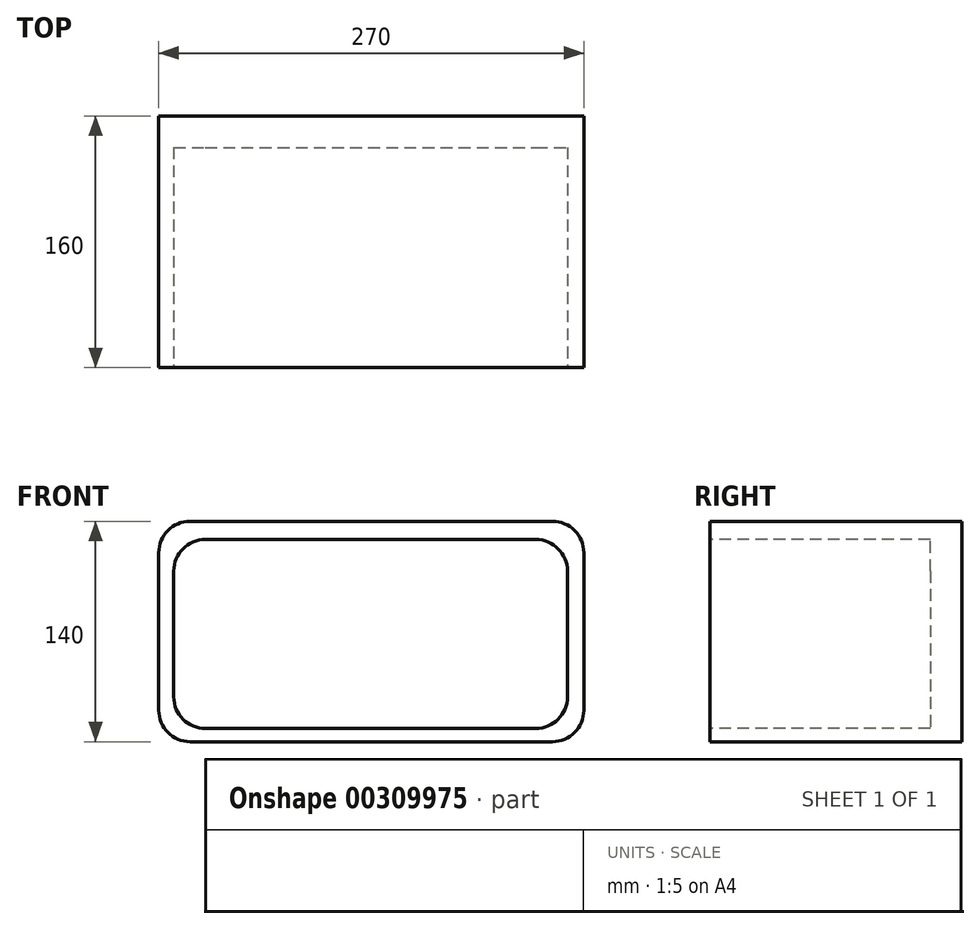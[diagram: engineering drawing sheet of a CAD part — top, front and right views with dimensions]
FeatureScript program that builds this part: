
annotation { "Feature Type Name" : "Feature", "Feature Type Description" : "" }
export const myFeature = defineFeature(function(context is Context, id is Id, definition is map)
    precondition{}
    {
        {
            var Q0;
            Q0=qCreatedBy(makeId("Front.planeOp"),FACE);
            var sketch = newSketch(context, id + "F0", { "sketchPlane" : qUnion([Q0])});
            skLineSegment(sketch, "E0.bottom", {"start": v(-135, 70) * mm, "end": v(135, 70) * mm});
            skLineSegment(sketch, "E0.top", {"start": v(-135, -70) * mm, "end": v(135, -70) * mm});
            skLineSegment(sketch, "E0.left", {"start": v(-135, 70) * mm, "end": v(-135, -70) * mm});
            skLineSegment(sketch, "E0.right", {"start": v(135, 70) * mm, "end": v(135, -70) * mm});
            skPoint(sketch, "E0.middle", {"position": v(0, 0) * mm});
            skSolve(sketch);
        }
        {
            var Q0;
            Q0=qSketchRegion(id+"F0",true);
            extrude(context, id + "F1", {"entities" : qUnion([Q0]), "depth" : 160 * mm});
        }
        {
            var Q0;
            Q0=makeQuery(id+"F1.opExtrude","CAP_FACE",FACE,{"disambiguationData":[OSD([sQuery(id+"F0.wireOp",EDGE,"E0.bottom"),sQuery(id+"F0.wireOp",EDGE,"E0.top"),sQuery(id+"F0.wireOp",EDGE,"E0.left"),sQuery(id+"F0.wireOp",EDGE,"E0.right")])],"isStart":false});
            var sketch = newSketch(context, id + "F2", { "sketchPlane" : qUnion([Q0])});
            skLineSegment(sketch, "E1.bottom", {"start": v(-125.42, 58.4) * mm, "end": v(124.58, 58.4) * mm});
            skLineSegment(sketch, "E1.top", {"start": v(-125.42, -61.6) * mm, "end": v(124.58, -61.6) * mm});
            skLineSegment(sketch, "E1.left", {"start": v(-125.42, 58.4) * mm, "end": v(-125.42, -61.6) * mm});
            skLineSegment(sketch, "E1.right", {"start": v(124.58, 58.4) * mm, "end": v(124.58, -61.6) * mm});
            skSolve(sketch);
        }
        {
            var Q0;
            Q0=qSketchRegion(id+"F2",true);
            extrude(context, id + "F3", {"entities" : qUnion([Q0]), "operationType" : NewBodyOperationType.REMOVE, "oppositeDirection" : true, "depth" : 140 * mm});
        }
        {
            var Q0;
            Q0=makeQuery(id+"F1.opExtrude","SWEPT_EDGE",EDGE,{"disambiguationData":[OSD([sQuery(id+"F0.wireOp",EDGE,"E0.bottom"),sQuery(id+"F0.wireOp",EDGE,"E0.right")])]});
            var Q1;
            Q1=makeQuery(id+"F1.opExtrude","SWEPT_EDGE",EDGE,{"disambiguationData":[OSD([sQuery(id+"F0.wireOp",EDGE,"E0.top"),sQuery(id+"F0.wireOp",EDGE,"E0.right")])]});
            var Q2;
            Q2=makeQuery(id+"F1.opExtrude","SWEPT_EDGE",EDGE,{"disambiguationData":[OSD([sQuery(id+"F0.wireOp",EDGE,"E0.bottom"),sQuery(id+"F0.wireOp",EDGE,"E0.left")])]});
            var Q3;
            Q3=makeQuery(id+"F1.opExtrude","SWEPT_EDGE",EDGE,{"disambiguationData":[OSD([sQuery(id+"F0.wireOp",EDGE,"E0.top"),sQuery(id+"F0.wireOp",EDGE,"E0.left")])]});
            var Q4;
            Q4=makeQuery(id+"F3.boolean.opBoolean","COPY",EDGE,{"derivedFrom":makeQuery(id+"F3.opExtrude","SWEPT_EDGE",EDGE,{"disambiguationData":[OSD([sQuery(id+"F2.wireOp",EDGE,"E1.top"),sQuery(id+"F2.wireOp",EDGE,"E1.right")])]})});
            var Q5;
            Q5=makeQuery(id+"F3.boolean.opBoolean","COPY",EDGE,{"derivedFrom":makeQuery(id+"F3.opExtrude","SWEPT_EDGE",EDGE,{"disambiguationData":[OSD([sQuery(id+"F2.wireOp",EDGE,"E1.bottom"),sQuery(id+"F2.wireOp",EDGE,"E1.right")])]})});
            var Q6;
            Q6=makeQuery(id+"F3.boolean.opBoolean","COPY",EDGE,{"derivedFrom":makeQuery(id+"F3.opExtrude","SWEPT_EDGE",EDGE,{"disambiguationData":[OSD([sQuery(id+"F2.wireOp",EDGE,"E1.bottom"),sQuery(id+"F2.wireOp",EDGE,"E1.left")])]})});
            var Q7;
            Q7=makeQuery(id+"F3.boolean.opBoolean","COPY",EDGE,{"derivedFrom":makeQuery(id+"F3.opExtrude","SWEPT_EDGE",EDGE,{"disambiguationData":[OSD([sQuery(id+"F2.wireOp",EDGE,"E1.top"),sQuery(id+"F2.wireOp",EDGE,"E1.left")])]})});
            fillet(context, id + "F4", {"entities" : qUnion([Q0, Q1, Q2, Q3, Q4, Q5, Q6, Q7]), "radius" : 20 * mm, "tangentPropagation" : true, "allowEdgeOverflow" : false});
        }
    });
